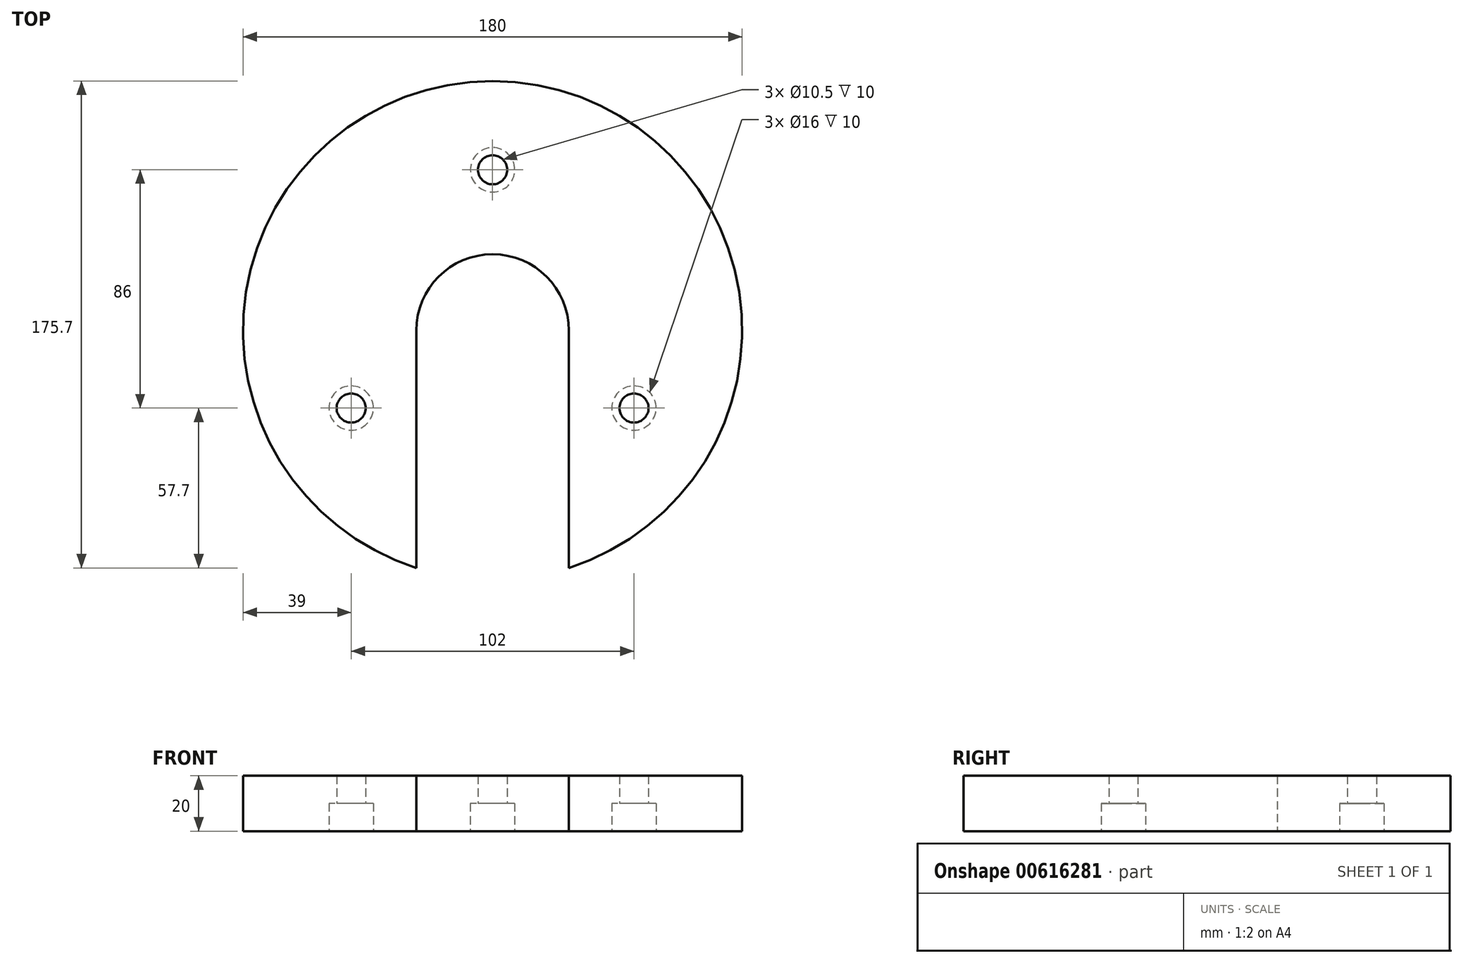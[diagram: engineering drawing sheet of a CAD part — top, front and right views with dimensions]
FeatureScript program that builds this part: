
annotation { "Feature Type Name" : "Feature", "Feature Type Description" : "" }
export const myFeature = defineFeature(function(context is Context, id is Id, definition is map)
    precondition{}
    {
        {
            var Q0;
            Q0=qCreatedBy(makeId("Top.planeOp"),FACE);
            var sketch = newSketch(context, id + "F0", { "sketchPlane" : qUnion([Q0])});
            skCircle(sketch, "E0", {"center": v(0, 0) * mm, "radius": 90 * mm});
            skCircle(sketch, "E1", {"center": v(0, 0) * mm, "radius": 27.5 * mm});
            skLineSegment(sketch, "E2", {"start": v(-27.5, 0) * mm, "end": v(-27.5, -85.7) * mm});
            skLineSegment(sketch, "E3", {"start": v(27.5, 0) * mm, "end": v(27.5, -85.7) * mm});
            skCircle(sketch, "E4", {"center": v(0, 58) * mm, "radius": 5.25 * mm});
            skCircle(sketch, "E5", {"center": v(-51, -28) * mm, "radius": 5.25 * mm});
            skCircle(sketch, "E6", {"center": v(51, -28) * mm, "radius": 5.25 * mm});
            skCircle(sketch, "E7", {"center": v(0, 58) * mm, "radius": 8 * mm});
            skCircle(sketch, "E8", {"center": v(-51, -28) * mm, "radius": 8 * mm});
            skCircle(sketch, "E9", {"center": v(51, -28) * mm, "radius": 8 * mm});
            skSolve(sketch);
        }
        {
            var Q0;
            {var subQ1=sQuery(id+"F0.wireOp",EDGE,"E2");Q0=makeQuery(id+"F0.imprint","IMPRINT",FACE,{"disambiguationData":[TD([[makeQuery(id+"F0.imprint","IMPRINT",EDGE,{"derivedFrom":subQ1}),-1.0]])]});}
            var Q1;
            Q1=makeQuery(id+"F0.imprint","IMPRINT",FACE,{"disambiguationData":[TD([[makeQuery(id+"F0.imprint","IMPRINT",EDGE,{"derivedFrom":sQuery(id+"F0.wireOp",EDGE,"E5")}),1.0]])]});
            var Q2;
            Q2=makeQuery(id+"F0.imprint","IMPRINT",FACE,{"disambiguationData":[TD([[makeQuery(id+"F0.imprint","IMPRINT",EDGE,{"derivedFrom":sQuery(id+"F0.wireOp",EDGE,"E5")}),-1.0]])]});
            var Q3;
            Q3=makeQuery(id+"F0.imprint","IMPRINT",FACE,{"disambiguationData":[TD([[makeQuery(id+"F0.imprint","IMPRINT",EDGE,{"derivedFrom":sQuery(id+"F0.wireOp",EDGE,"E6")}),-1.0]])]});
            var Q4;
            Q4=makeQuery(id+"F0.imprint","IMPRINT",FACE,{"disambiguationData":[TD([[makeQuery(id+"F0.imprint","IMPRINT",EDGE,{"derivedFrom":sQuery(id+"F0.wireOp",EDGE,"E6")}),1.0]])]});
            var Q5;
            Q5=makeQuery(id+"F0.imprint","IMPRINT",FACE,{"disambiguationData":[TD([[makeQuery(id+"F0.imprint","IMPRINT",EDGE,{"derivedFrom":sQuery(id+"F0.wireOp",EDGE,"E4")}),-1.0]])]});
            var Q6;
            Q6=makeQuery(id+"F0.imprint","IMPRINT",FACE,{"disambiguationData":[TD([[makeQuery(id+"F0.imprint","IMPRINT",EDGE,{"derivedFrom":sQuery(id+"F0.wireOp",EDGE,"E4")}),1.0]])]});
            extrude(context, id + "F1", {"entities" : qUnion([Q0, Q1, Q2, Q3, Q4, Q5, Q6]), "depth" : 20 * mm, "offsetDistance" : 25 * mm});
        }
        {
            var Q0;
            Q0=makeQuery(id+"F0.imprint","IMPRINT",FACE,{"disambiguationData":[TD([[makeQuery(id+"F0.imprint","IMPRINT",EDGE,{"derivedFrom":sQuery(id+"F0.wireOp",EDGE,"E4")}),1.0]])]});
            var Q1;
            Q1=makeQuery(id+"F0.imprint","IMPRINT",FACE,{"disambiguationData":[TD([[makeQuery(id+"F0.imprint","IMPRINT",EDGE,{"derivedFrom":sQuery(id+"F0.wireOp",EDGE,"E5")}),1.0]])]});
            var Q2;
            Q2=makeQuery(id+"F0.imprint","IMPRINT",FACE,{"disambiguationData":[TD([[makeQuery(id+"F0.imprint","IMPRINT",EDGE,{"derivedFrom":sQuery(id+"F0.wireOp",EDGE,"E6")}),1.0]])]});
            extrude(context, id + "F2", {"entities" : qUnion([Q0, Q1, Q2]), "operationType" : NewBodyOperationType.REMOVE, "endBound" : BoundingType.THROUGH_ALL, "depth" : 25 * mm, "offsetDistance" : 25 * mm});
        }
        {
            var Q0;
            Q0=makeQuery(id+"F0.imprint","IMPRINT",FACE,{"disambiguationData":[TD([[makeQuery(id+"F0.imprint","IMPRINT",EDGE,{"derivedFrom":sQuery(id+"F0.wireOp",EDGE,"E4")}),-1.0]])]});
            var Q1;
            Q1=makeQuery(id+"F0.imprint","IMPRINT",FACE,{"disambiguationData":[TD([[makeQuery(id+"F0.imprint","IMPRINT",EDGE,{"derivedFrom":sQuery(id+"F0.wireOp",EDGE,"E6")}),-1.0]])]});
            var Q2;
            Q2=makeQuery(id+"F0.imprint","IMPRINT",FACE,{"disambiguationData":[TD([[makeQuery(id+"F0.imprint","IMPRINT",EDGE,{"derivedFrom":sQuery(id+"F0.wireOp",EDGE,"E5")}),-1.0]])]});
            extrude(context, id + "F3", {"entities" : qUnion([Q0, Q1, Q2]), "operationType" : NewBodyOperationType.REMOVE, "depth" : 10 * mm, "offsetDistance" : 25 * mm});
        }
    });
